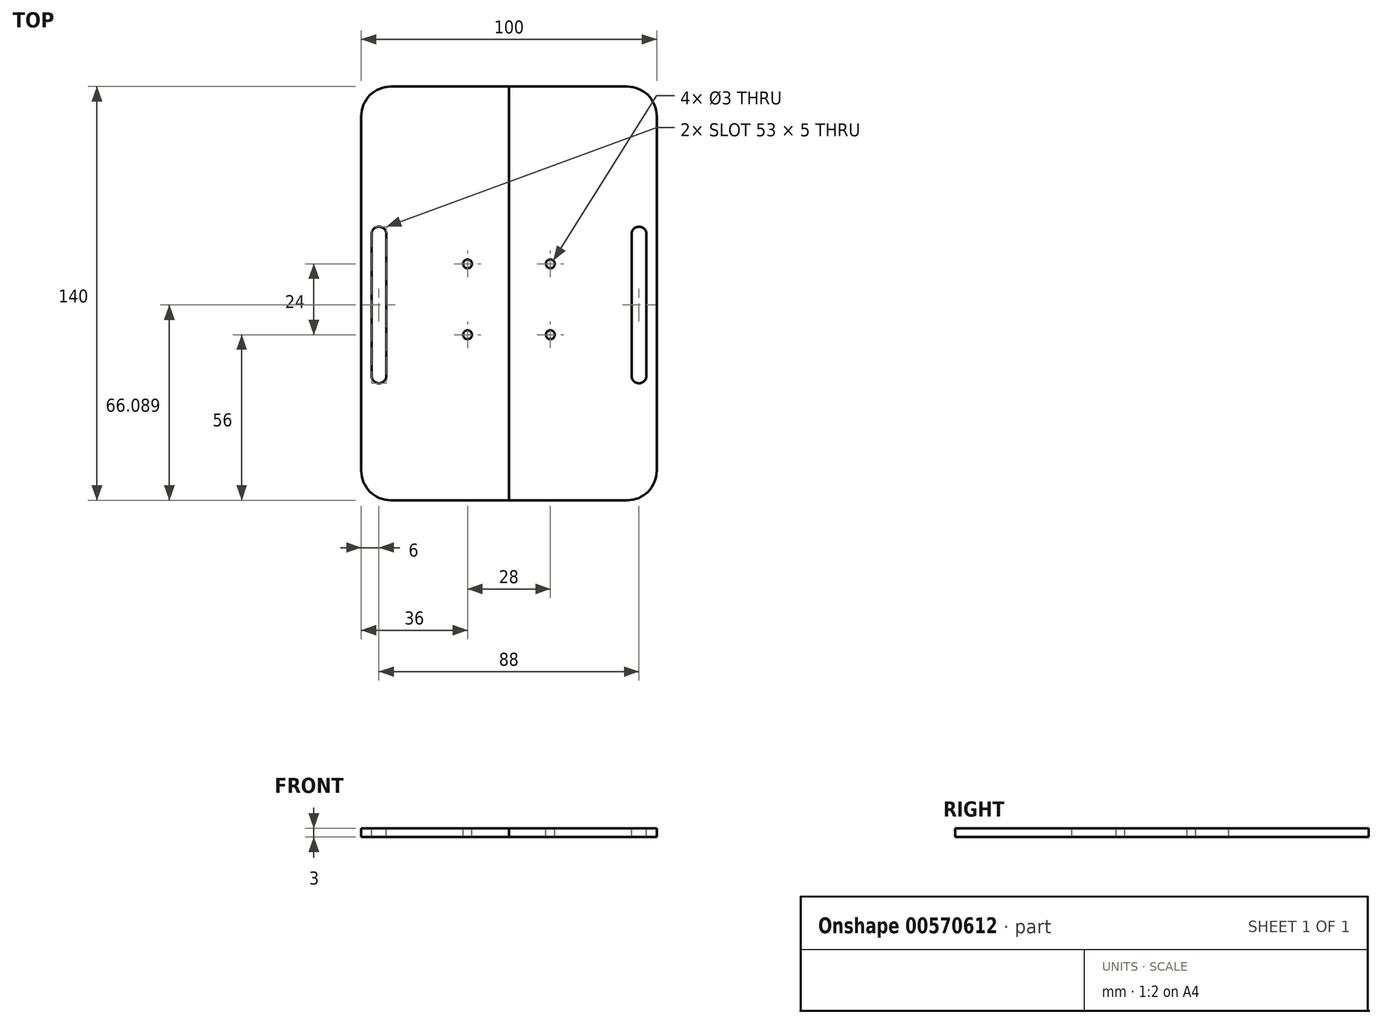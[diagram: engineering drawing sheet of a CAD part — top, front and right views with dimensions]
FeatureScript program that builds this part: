
annotation { "Feature Type Name" : "Feature", "Feature Type Description" : "" }
export const myFeature = defineFeature(function(context is Context, id is Id, definition is map)
    precondition{}
    {
        {
            var Q0;
            Q0=qCreatedBy(makeId("Top.planeOp"),FACE);
            var sketch = newSketch(context, id + "F0", { "sketchPlane" : qUnion([Q0])});
            skLineSegment(sketch, "E0.bottom", {"start": v(0, 0) * mm, "end": v(50, 0) * mm});
            skLineSegment(sketch, "E0.top", {"start": v(0, 140) * mm, "end": v(50, 140) * mm});
            skLineSegment(sketch, "E0.left", {"start": v(0, 0) * mm, "end": v(0, 140) * mm});
            skLineSegment(sketch, "E0.right", {"start": v(50, 0) * mm, "end": v(50, 140) * mm});
            skSolve(sketch);
        }
        {
            var Q0;
            Q0=makeQuery(id+"F0.imprint","IMPRINT",FACE,{"disambiguationData":[TD([[makeQuery(id+"F0.imprint","IMPRINT",EDGE,{"derivedFrom":sQuery(id+"F0.wireOp",EDGE,"E0.bottom")}),1.0]])]});
            var sketch = newSketch(context, id + "F1", { "sketchPlane" : qUnion([Q0])});
            skSolve(sketch);
        }
        {
            var Q0;
            Q0=makeQuery(id+"F1.imprint","IMPRINT",FACE,{"disambiguationData":[TD([[makeQuery(id+"F1.imprint","IMPRINT",EDGE,{"derivedFrom":makeQuery(id+"F0.imprint","IMPRINT",EDGE,{"derivedFrom":sQuery(id+"F0.wireOp",EDGE,"E0.bottom")})}),1.0]])]});
            extrude(context, id + "F2", {"entities" : qUnion([Q0]), "depth" : 3 * mm, "offsetDistance" : 25 * mm});
        }
        {
            var Q0;
            Q0=makeQuery(id+"F2.opExtrude","CAP_FACE",FACE,{"disambiguationData":[OSD([sQuery(id+"F0.wireOp",EDGE,"E0.bottom"),sQuery(id+"F0.wireOp",EDGE,"E0.top"),sQuery(id+"F0.wireOp",EDGE,"E0.left"),sQuery(id+"F0.wireOp",EDGE,"E0.right")])],"isStart":false});
            var sketch = newSketch(context, id + "F3", { "sketchPlane" : qUnion([Q0])});
            skLineSegment(sketch, "E1", {"start": v(14, 80) * mm, "end": v(14, 56) * mm});
            skSolve(sketch);
        }
        {
            var Q0;
            Q0=sQuery(id+"F3.wireOp",VERTEX,"E1.start");
            var Q1;
            Q1=sQuery(id+"F3.wireOp",VERTEX,"E1.end");
            var Q2;
            Q2=makeQuery(id+"F2.opExtrude","SWEPT_BODY",BODY,{"disambiguationData":[OSD([sQuery(id+"F0.wireOp",EDGE,"E0.bottom"),sQuery(id+"F0.wireOp",EDGE,"E0.top"),sQuery(id+"F0.wireOp",EDGE,"E0.left"),sQuery(id+"F0.wireOp",EDGE,"E0.right")])]});
            hole(context, id + "F4", {"style" : HoleStyle.SIMPLE, "endStyle" : HoleEndStyle.THROUGH, "holeDiameter" : 3 * mm, "isTappedThrough" : true, "tappedDepth" : 12 * mm, "tapClearance" : 3, "locations" : qUnion([Q0, Q1]), "scope" : qUnion([Q2])});
        }
        {
            var Q0;
            Q0=makeQuery(id+"F2.opExtrude","CAP_FACE",FACE,{"disambiguationData":[OSD([sQuery(id+"F0.wireOp",EDGE,"E0.bottom"),sQuery(id+"F0.wireOp",EDGE,"E0.top"),sQuery(id+"F0.wireOp",EDGE,"E0.left"),sQuery(id+"F0.wireOp",EDGE,"E0.right")])],"isStart":false});
            var sketch = newSketch(context, id + "F5", { "sketchPlane" : qUnion([Q0])});
            skLineSegment(sketch, "E2", {"start": v(50, 42.09) * mm, "end": v(50, 90.09) * mm});
            skLineSegment(sketch, "E3", {"start": v(44, 90.09) * mm, "end": v(44, 42.09) * mm});
            skSolve(sketch);
        }
        {
            var Q0;
            {var subQ2=sQuery(id+"F5.wireOp",EDGE,"E2");Q0=makeQuery(id+"F5.imprint","IMPRINT",FACE,{"disambiguationData":[TD([[makeQuery(id+"F5.imprint","IMPRINT",EDGE,{"derivedFrom":subQ2}),1.0]])]});}
            var sketch = newSketch(context, id + "F6", { "sketchPlane" : qUnion([Q0])});
            skLineSegment(sketch, "E4.JWF.JWF", {"start": v(44, 90.09) * mm, "end": v(44, 42.09) * mm, "construction": true});
            skArc(sketch, "E4.0.startCap", {"start": v(41.5, 90.09) * mm, "mid": v(44, 92.59) * mm, "end": v(46.5, 90.09) * mm});
            skArc(sketch, "E4.0.endCap", {"start": v(46.5, 42.09) * mm, "mid": v(44, 39.59) * mm, "end": v(41.5, 42.09) * mm});
            skLineSegment(sketch, "E4.0.left", {"start": v(46.5, 90.09) * mm, "end": v(46.5, 42.09) * mm});
            skLineSegment(sketch, "E4.0.right", {"start": v(41.5, 90.09) * mm, "end": v(41.5, 42.09) * mm});
            skSolve(sketch);
        }
        {
            var Q0;
            Q0 = qSketchRegion(id + "F6", true);
            extrude(context, id + "F7", {"entities" : qUnion([Q0]), "operationType" : NewBodyOperationType.REMOVE, "oppositeDirection" : true, "depth" : 40.84 * mm, "offsetDistance" : 25 * mm});
        }
        {
            var Q0;
            Q0=makeQuery(id+"F2.opExtrude","SWEPT_EDGE",EDGE,{"disambiguationData":[OSD([sQuery(id+"F0.wireOp",EDGE,"E0.top"),sQuery(id+"F0.wireOp",EDGE,"E0.right")])]});
            var Q1;
            Q1=makeQuery(id+"F2.opExtrude","SWEPT_EDGE",EDGE,{"disambiguationData":[OSD([sQuery(id+"F0.wireOp",EDGE,"E0.bottom"),sQuery(id+"F0.wireOp",EDGE,"E0.right")])]});
            fillet(context, id + "F8", {"entities" : qUnion([Q0, Q1]), "radius" : 10 * mm, "tangentPropagation" : true, "allowEdgeOverflow" : false});
        }
        {
            var Q0;
            Q0=makeQuery(id+"F2.opExtrude","SWEPT_BODY",BODY,{"disambiguationData":[OSD([sQuery(id+"F0.wireOp",EDGE,"E0.bottom"),sQuery(id+"F0.wireOp",EDGE,"E0.top"),sQuery(id+"F0.wireOp",EDGE,"E0.left"),sQuery(id+"F0.wireOp",EDGE,"E0.right")])]});
            var Q1;
            Q1=qCreatedBy(makeId("Right.planeOp"),FACE);
            mirror(context, id + "F9", {"entities" : qUnion([Q0]), "mirrorPlane" : qUnion([Q1])});
        }
    });
